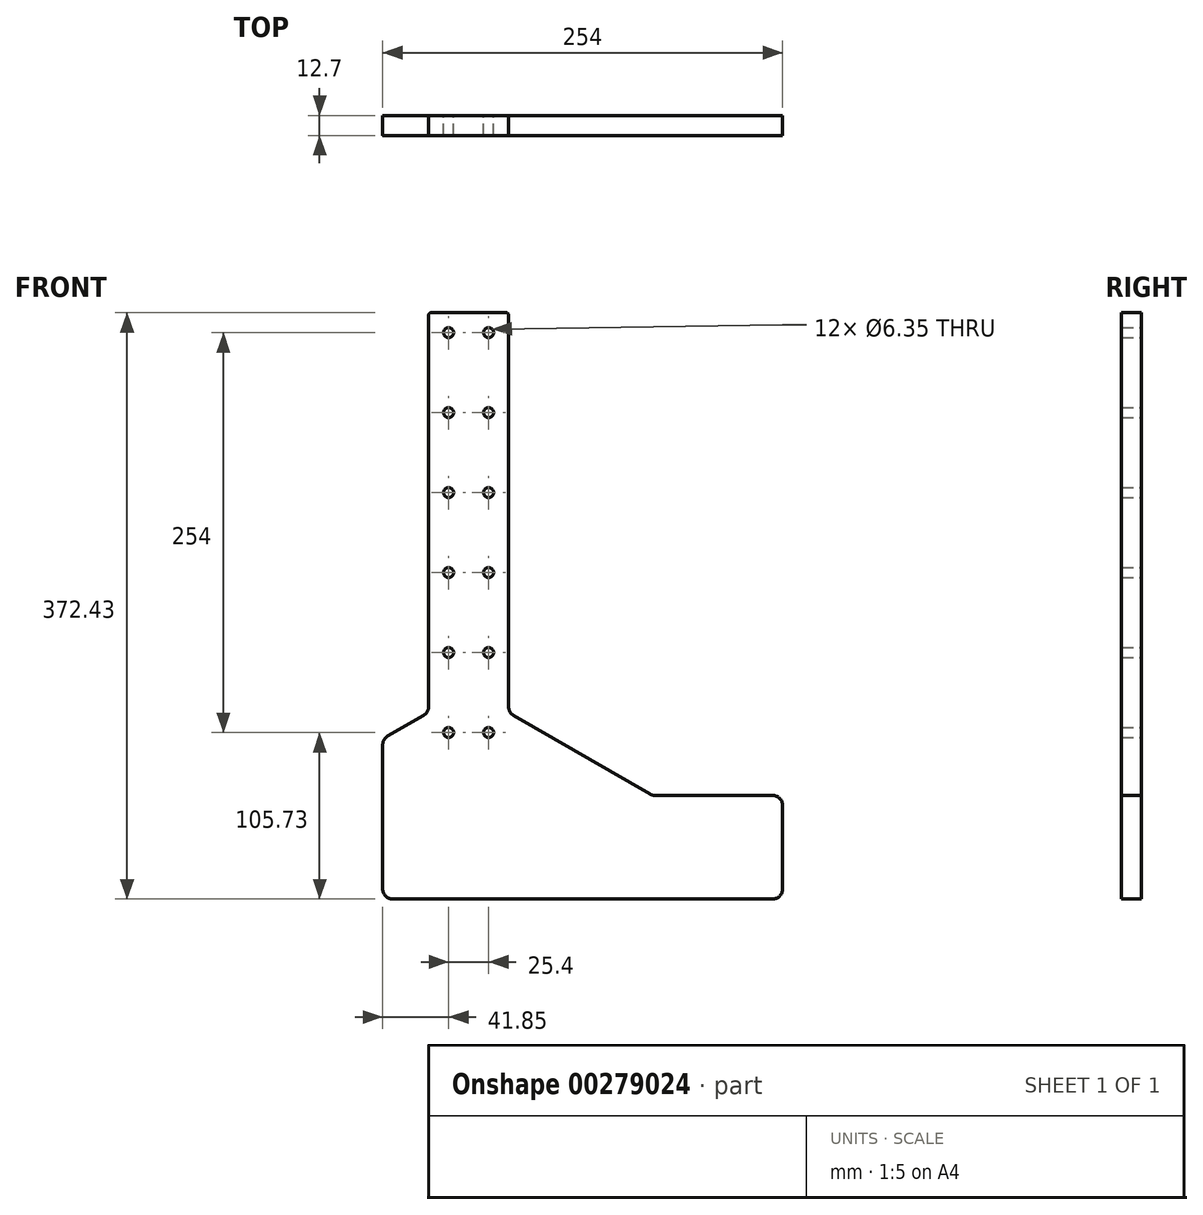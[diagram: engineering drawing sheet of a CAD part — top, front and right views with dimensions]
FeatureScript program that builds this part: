
annotation { "Feature Type Name" : "Feature", "Feature Type Description" : "" }
export const myFeature = defineFeature(function(context is Context, id is Id, definition is map)
    precondition{}
    {
        {
            var Q0;
            Q0=qCreatedBy(makeId("Front.planeOp"),FACE);
            var sketch = newSketch(context, id + "F0", { "sketchPlane" : qUnion([Q0])});
            skLineSegment(sketch, "E0", {"start": v(-23.81, 0) * mm, "end": v(23.81, 0) * mm});
            skLineSegment(sketch, "E1", {"start": v(-25.4, -1.59) * mm, "end": v(-25.4, -250.33) * mm});
            skLineSegment(sketch, "E2", {"start": v(25.4, -1.59) * mm, "end": v(25.4, -250.33) * mm});
            skLineSegment(sketch, "E3", {"start": v(28.57, -255.83) * mm, "end": v(115.1, -305.8) * mm});
            skLineSegment(sketch, "E4", {"start": v(25.4, -254) * mm, "end": v(25.4, -256.9) * mm, "construction": true});
            skLineSegment(sketch, "E5", {"start": v(-28.58, -255.83) * mm, "end": v(-51.37, -269) * mm});
            skLineSegment(sketch, "E6", {"start": v(-25.4, -254) * mm, "end": v(-25.4, -288.8) * mm, "construction": true});
            skLineSegment(sketch, "E7", {"start": v(-54.55, -274.5) * mm, "end": v(-54.55, -366.08) * mm});
            skLineSegment(sketch, "E8", {"start": v(-48.2, -372.43) * mm, "end": v(193.1, -372.43) * mm});
            skLineSegment(sketch, "E9", {"start": v(199.45, -366.08) * mm, "end": v(199.45, -313) * mm});
            skLineSegment(sketch, "E10", {"start": v(193.1, -306.64) * mm, "end": v(118.28, -306.64) * mm});
            skPoint(sketch, "E11.visualSharp", {"position": v(-54.55, -270.83) * mm});
            skArc(sketch, "E11.filletArc", {"start": v(-51.37, -269) * mm, "mid": v(-53.7, -271.32) * mm, "end": v(-54.55, -274.5) * mm});
            skPoint(sketch, "E12.visualSharp", {"position": v(-25.4, -254) * mm});
            skArc(sketch, "E12.filletArc", {"start": v(-28.57, -255.83) * mm, "mid": v(-26.25, -253.5) * mm, "end": v(-25.4, -250.33) * mm});
            skPoint(sketch, "E13.visualSharp", {"position": v(25.4, -254) * mm});
            skArc(sketch, "E13.filletArc", {"start": v(25.4, -250.33) * mm, "mid": v(26.25, -253.5) * mm, "end": v(28.58, -255.83) * mm});
            skPoint(sketch, "E14.visualSharp", {"position": v(116.58, -306.64) * mm});
            skArc(sketch, "E14.filletArc", {"start": v(115.1, -305.8) * mm, "mid": v(116.64, -306.43) * mm, "end": v(118.28, -306.64) * mm});
            skPoint(sketch, "E15.visualSharp", {"position": v(199.45, -306.64) * mm});
            skArc(sketch, "E15.filletArc", {"start": v(199.45, -313) * mm, "mid": v(197.6, -308.5) * mm, "end": v(193.1, -306.64) * mm});
            skPoint(sketch, "E16.visualSharp", {"position": v(199.45, -372.43) * mm});
            skArc(sketch, "E16.filletArc", {"start": v(193.1, -372.43) * mm, "mid": v(197.6, -370.57) * mm, "end": v(199.45, -366.08) * mm});
            skPoint(sketch, "E17.visualSharp", {"position": v(-54.55, -372.43) * mm});
            skArc(sketch, "E17.filletArc", {"start": v(-54.55, -366.08) * mm, "mid": v(-52.69, -370.57) * mm, "end": v(-48.2, -372.43) * mm});
            skPoint(sketch, "E18.visualSharp", {"position": v(-25.4, 0) * mm});
            skArc(sketch, "E18.filletArc", {"start": v(-23.81, 0) * mm, "mid": v(-24.94, -0.46) * mm, "end": v(-25.4, -1.59) * mm});
            skPoint(sketch, "E19.visualSharp", {"position": v(25.4, 0) * mm});
            skArc(sketch, "E19.filletArc", {"start": v(25.4, -1.59) * mm, "mid": v(24.94, -0.46) * mm, "end": v(23.81, 0) * mm});
            skLineSegment(sketch, "E20.0", {"start": v(-23.81, -12.7) * mm, "end": v(23.81, -12.7) * mm, "construction": true});
            skLineSegment(sketch, "E21.0", {"start": v(12.7, -1.59) * mm, "end": v(12.7, -296.14) * mm, "construction": true});
            skLineSegment(sketch, "E22.0", {"start": v(-12.7, -1.59) * mm, "end": v(-12.7, -296.14) * mm, "construction": true});
            skLineSegment(sketch, "E23.0", {"start": v(-23.81, -63.5) * mm, "end": v(23.81, -63.5) * mm, "construction": true});
            skLineSegment(sketch, "E24.0", {"start": v(-23.81, -114.3) * mm, "end": v(23.81, -114.3) * mm, "construction": true});
            skLineSegment(sketch, "E25.0", {"start": v(-23.81, -165.1) * mm, "end": v(23.81, -165.1) * mm, "construction": true});
            skLineSegment(sketch, "E26.0", {"start": v(-23.81, -215.9) * mm, "end": v(23.81, -215.9) * mm, "construction": true});
            skLineSegment(sketch, "E27.0", {"start": v(-23.81, -266.7) * mm, "end": v(23.81, -266.7) * mm, "construction": true});
            skCircle(sketch, "E28", {"center": v(-12.7, -266.7) * mm, "radius": 3.18 * mm});
            skCircle(sketch, "E29.0.1.0", {"center": v(-12.7, -215.9) * mm, "radius": 3.18 * mm});
            skCircle(sketch, "E29.0.2.0", {"center": v(-12.7, -165.1) * mm, "radius": 3.18 * mm});
            skCircle(sketch, "E29.0.3.0", {"center": v(-12.7, -114.3) * mm, "radius": 3.18 * mm});
            skCircle(sketch, "E29.0.4.0", {"center": v(-12.7, -63.5) * mm, "radius": 3.18 * mm});
            skCircle(sketch, "E29.0.5.0", {"center": v(-12.7, -12.7) * mm, "radius": 3.18 * mm});
            skCircle(sketch, "E29.1.0.0", {"center": v(12.7, -266.7) * mm, "radius": 3.18 * mm});
            skCircle(sketch, "E29.1.1.0", {"center": v(12.7, -215.9) * mm, "radius": 3.18 * mm});
            skCircle(sketch, "E29.1.2.0", {"center": v(12.7, -165.1) * mm, "radius": 3.18 * mm});
            skCircle(sketch, "E29.1.3.0", {"center": v(12.7, -114.3) * mm, "radius": 3.18 * mm});
            skCircle(sketch, "E29.1.4.0", {"center": v(12.7, -63.5) * mm, "radius": 3.18 * mm});
            skCircle(sketch, "E29.1.5.0", {"center": v(12.7, -12.7) * mm, "radius": 3.18 * mm});
            skLineSegment(sketch, "E29.direction1", {"start": v(-12.7, -266.7) * mm, "end": v(12.7, -266.7) * mm, "construction": true});
            skLineSegment(sketch, "E29.direction2", {"start": v(-12.7, -266.7) * mm, "end": v(-12.7, -215.9) * mm, "construction": true});
            skLineSegment(sketch, "E30", {"start": v(-54.55, -270.83) * mm, "end": v(208.75, -270.83) * mm, "construction": true});
            skSolve(sketch);
        }
        {
            var Q0;
            Q0=makeQuery(id+"F0.imprint","IMPRINT",FACE,{"disambiguationData":[TD([[makeQuery(id+"F0.imprint","IMPRINT",EDGE,{"derivedFrom":sQuery(id+"F0.wireOp",EDGE,"E0")}),-1.0]])]});
            extrude(context, id + "F1", {"entities" : qUnion([Q0]), "endBound" : BoundingType.SYMMETRIC, "depth" : 12.7 * mm});
        }
    });
